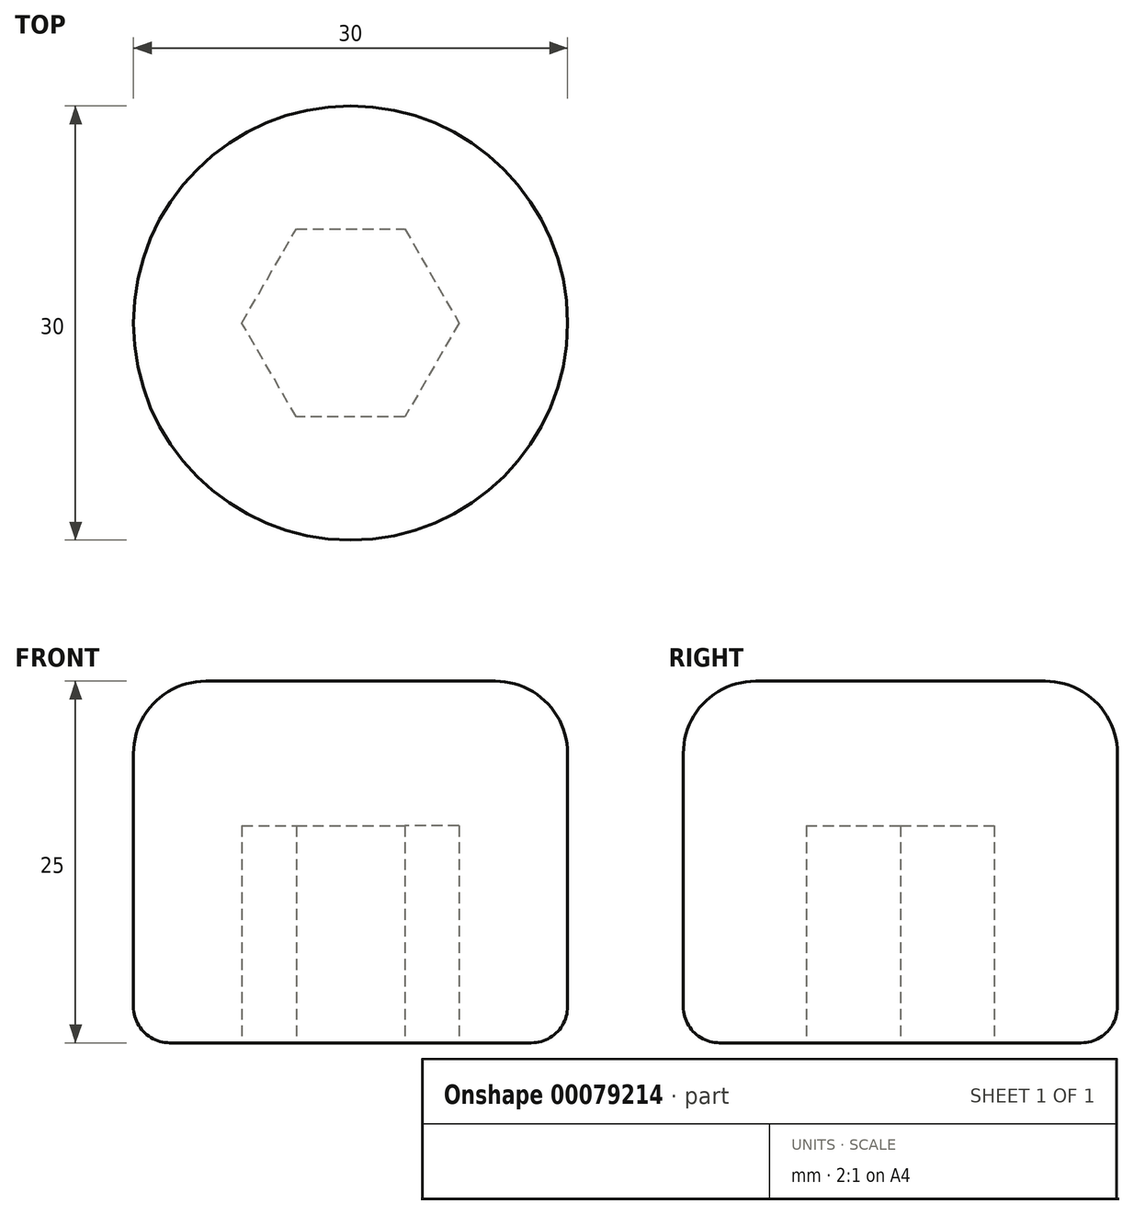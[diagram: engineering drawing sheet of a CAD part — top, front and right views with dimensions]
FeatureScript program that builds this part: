
annotation { "Feature Type Name" : "Feature", "Feature Type Description" : "" }
export const myFeature = defineFeature(function(context is Context, id is Id, definition is map)
    precondition{}
    {
        {
            var Q0;
            Q0=qCreatedBy(makeId("Top.planeOp"),FACE);
            var sketch = newSketch(context, id + "F0", { "sketchPlane" : qUnion([Q0])});
            skCircle(sketch, "E0.cCircle", {"center": v(0, 0) * mm, "radius": 6.5 * mm, "construction": true});
            skLineSegment(sketch, "E0.0", {"start": v(-3.75, 6.5) * mm, "end": v(3.75, 6.5) * mm});
            skLineSegment(sketch, "E0.1", {"start": v(3.75, 6.5) * mm, "end": v(7.5, 0) * mm});
            skLineSegment(sketch, "E0.2", {"start": v(7.5, 0) * mm, "end": v(3.75, -6.5) * mm});
            skLineSegment(sketch, "E0.3", {"start": v(3.75, -6.5) * mm, "end": v(-3.75, -6.5) * mm});
            skLineSegment(sketch, "E0.4", {"start": v(-3.75, -6.5) * mm, "end": v(-7.5, 0) * mm});
            skLineSegment(sketch, "E0.5", {"start": v(-7.5, 0) * mm, "end": v(-3.75, 6.5) * mm});
            skPoint(sketch, "E0.0.midPoint", {"position": v(0, 6.5) * mm});
            skCircle(sketch, "E1", {"center": v(0, 0) * mm, "radius": 15 * mm});
            skSolve(sketch);
        }
        {
            var Q0;
            Q0=makeQuery(id+"F0.imprint","IMPRINT",FACE,{"disambiguationData":[TD([[makeQuery(id+"F0.imprint","IMPRINT",EDGE,{"derivedFrom":sQuery(id+"F0.wireOp",EDGE,"E0.0")}),1.0]])]});
            var Q1;
            Q1=makeQuery(id+"F0.imprint","IMPRINT",FACE,{"disambiguationData":[TD([[makeQuery(id+"F0.imprint","IMPRINT",EDGE,{"derivedFrom":sQuery(id+"F0.wireOp",EDGE,"E0.0")}),-1.0]])]});
            extrude(context, id + "F1", {"entities" : qUnion([Q0, Q1]), "depth" : 25 * mm});
        }
        {
            var Q0;
            Q0=makeQuery(id+"F1.opExtrude","CAP_EDGE",EDGE,{"disambiguationData":[OSD([sQuery(id+"F0.wireOp",EDGE,"E1")])],"isStart":false});
            fillet(context, id + "F2", {"entities" : qUnion([Q0]), "radius" : 5 * mm, "tangentPropagation" : true, "allowEdgeOverflow" : false});
        }
        {
            var Q0;
            Q0=makeQuery(id+"F1.opExtrude","CAP_EDGE",EDGE,{"disambiguationData":[OSD([sQuery(id+"F0.wireOp",EDGE,"E1")])],"isStart":true});
            fillet(context, id + "F3", {"entities" : qUnion([Q0]), "radius" : 2.5 * mm, "tangentPropagation" : true, "allowEdgeOverflow" : false});
        }
        {
            var Q0;
            Q0=makeQuery(id+"F0.imprint","IMPRINT",FACE,{"disambiguationData":[TD([[makeQuery(id+"F0.imprint","IMPRINT",EDGE,{"derivedFrom":sQuery(id+"F0.wireOp",EDGE,"E0.0")}),-1.0]])]});
            extrude(context, id + "F4", {"entities" : qUnion([Q0]), "operationType" : NewBodyOperationType.REMOVE, "depth" : 15 * mm});
        }
    });
